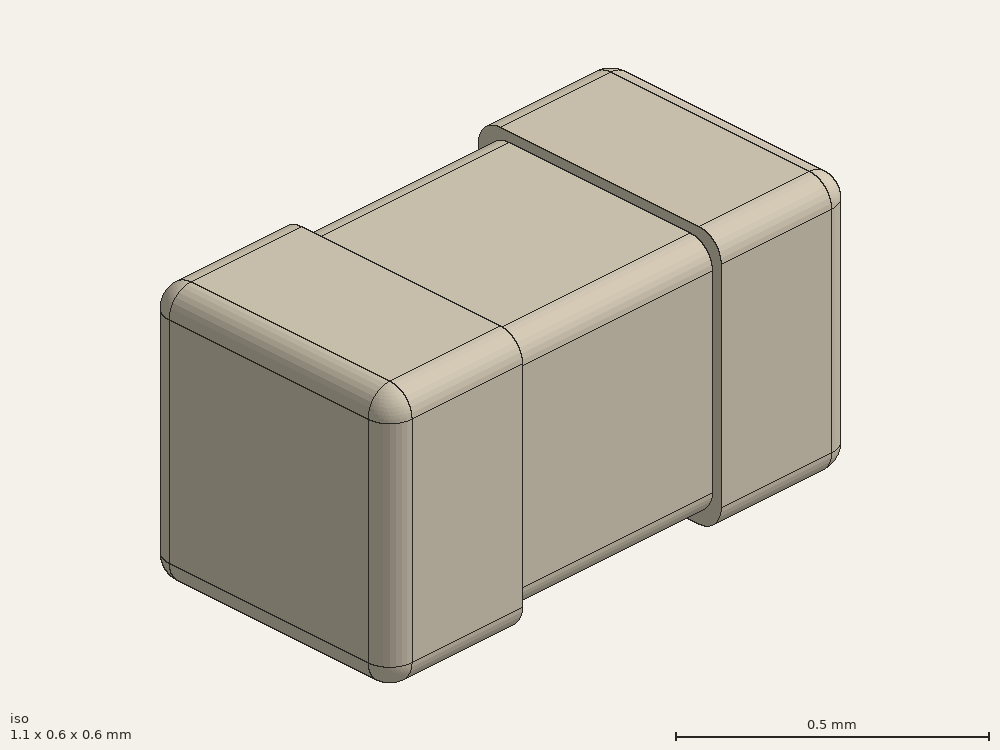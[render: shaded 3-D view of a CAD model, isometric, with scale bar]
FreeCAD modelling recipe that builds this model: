
FCSTD DOCUMENT
Label: CAP_CHIP_1005X050
Comment: Kemet C0402... / H0.5+-0.05
objects: Part::Box×3, Part::Fillet×3, Part::MultiFuse×1
note: 7 computed .brp shape members not serialized (recipe doc carries the construction recipe); baked Part::Feature solids carry a one-line shape summary decoded from their .brp

FEATURE [Part::Box] chip
  Height = 0.51
  Length = 1.01
  Placement = pos=(-0.505,-0.255,0.02) rot=(0,0,1;0rad)
  Width = 0.51
FEATURE [Part::Fillet] chip_f
  Base = -> chip
  Edges = 4 edges r=0.05: [Edge9,Edge10,Edge11,Edge12]
FEATURE [Part::Box] plating_left
  Height = 0.55
  Length = 0.3
  Placement = pos=(-0.525,-0.275,0) rot=(0,0,1;0rad)
  Width = 0.55
FEATURE [Part::Fillet] plating_left_f
  Base = -> plating_left
  Edges = 8 edges r=0.05: [Edge1,Edge2,Edge3,Edge4,Edge9,Edge10,Edge11,Edge12]
FEATURE [Part::Box] plating_right
  Height = 0.55
  Length = 0.3
  Placement = pos=(0.225,-0.275,0) rot=(0,0,1;0rad)
  Width = 0.55
FEATURE [Part::Fillet] plating_right_f
  Base = -> plating_right
  Edges = 8 edges r=0.05: [Edge5,Edge6,Edge7,Edge8,Edge9,Edge10,Edge11,Edge12]
FEATURE [Part::MultiFuse] capacitor
  Shapes = -> [chip_f,plating_left_f,plating_right_f]
